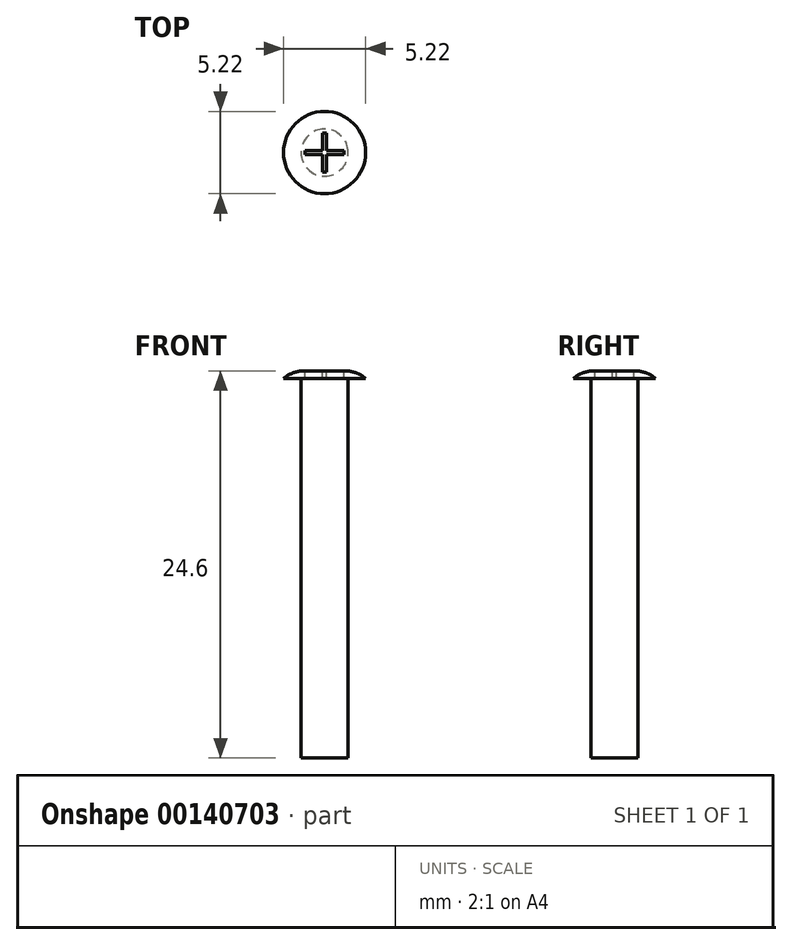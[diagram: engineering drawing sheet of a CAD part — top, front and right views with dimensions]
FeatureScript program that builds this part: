
annotation { "Feature Type Name" : "Feature", "Feature Type Description" : "" }
export const myFeature = defineFeature(function(context is Context, id is Id, definition is map)
    precondition{}
    {
        {
            var Q0;
            Q0=qCreatedBy(makeId("Top.planeOp"),FACE);
            var sketch = newSketch(context, id + "F0", { "sketchPlane" : qUnion([Q0])});
            skCircle(sketch, "E0", {"center": v(0, 0) * mm, "radius": 1.5 * mm});
            skSolve(sketch);
        }
        {
            var Q0;
            Q0=makeQuery(id+"F0.imprint","IMPRINT",FACE,{"disambiguationData":[TD([[makeQuery(id+"F0.imprint","IMPRINT",EDGE,{"derivedFrom":sQuery(id+"F0.wireOp",EDGE,"E0")}),1.0]])]});
            extrude(context, id + "F1", {"entities" : qUnion([Q0]), "depth" : 24.6 * mm});
        }
        {
            var Q0;
            Q0=makeQuery(id+"F1.opExtrude","CAP_FACE",FACE,{"disambiguationData":[OSD([sQuery(id+"F0.wireOp",EDGE,"E0")])],"isStart":false});
            var sketch = newSketch(context, id + "F2", { "sketchPlane" : qUnion([Q0])});
            skCircle(sketch, "E1.0", {"center": v(0, 0) * mm, "radius": 1.5 * mm});
            skCircle(sketch, "E2", {"center": v(0, 0) * mm, "radius": 2.6 * mm});
            skLineSegment(sketch, "E3", {"start": v(-1.25, -0.12) * mm, "end": v(-0.12, -0.12) * mm});
            skLineSegment(sketch, "E4", {"start": v(-1.25, 0.12) * mm, "end": v(-0.12, 0.12) * mm});
            skLineSegment(sketch, "E5", {"start": v(-0.12, -1.25) * mm, "end": v(-0.12, -0.12) * mm});
            skLineSegment(sketch, "E6", {"start": v(0.12, -1.25) * mm, "end": v(0.12, -0.12) * mm});
            skLineSegment(sketch, "E7.trimOffspring", {"start": v(-0.12, 0.12) * mm, "end": v(-0.12, 1.25) * mm});
            skLineSegment(sketch, "E8.trimOffspring", {"start": v(0.12, -0.12) * mm, "end": v(1.25, -0.12) * mm});
            skLineSegment(sketch, "E9.trimOffspring", {"start": v(0.12, 0.12) * mm, "end": v(1.25, 0.12) * mm});
            skLineSegment(sketch, "E10.trimOffspring", {"start": v(0.12, 0.12) * mm, "end": v(0.12, 1.25) * mm});
            skLineSegment(sketch, "E11", {"start": v(-1.25, -0.12) * mm, "end": v(-1.25, 0.12) * mm});
            skLineSegment(sketch, "E12", {"start": v(-0.12, -1.25) * mm, "end": v(0.12, -1.25) * mm});
            skLineSegment(sketch, "E13", {"start": v(1.25, -0.12) * mm, "end": v(1.25, 0.12) * mm});
            skLineSegment(sketch, "E14", {"start": v(-0.12, 1.25) * mm, "end": v(0.12, 1.25) * mm});
            skSolve(sketch);
        }
        {
            var Q0;
            Q0=qSketchRegion(id+"F2",true);
            extrude(context, id + "F3", {"entities" : qUnion([Q0]), "operationType" : NewBodyOperationType.ADD, "oppositeDirection" : true, "depth" : 0.5 * mm});
        }
        {
            var Q0;
            Q0=makeQuery(id+"F3.opExtrude","CAP_EDGE",EDGE,{"disambiguationData":[OSD([sQuery(id+"F2.wireOp",EDGE,"E2")])],"isStart":true});
            fillet(context, id + "F4", {"entities" : qUnion([Q0]), "radius" : 2 * mm, "tangentPropagation" : true, "allowEdgeOverflow" : false});
        }
        {
            var Q0;
            Q0=makeQuery(id+"F2.imprint","IMPRINT",FACE,{"disambiguationData":[TD([[makeQuery(id+"F2.imprint","IMPRINT",EDGE,{"derivedFrom":sQuery(id+"F2.wireOp",EDGE,"E3")}),1.0]])]});
            extrude(context, id + "F5", {"entities" : qUnion([Q0]), "operationType" : NewBodyOperationType.REMOVE, "oppositeDirection" : true, "depth" : 0.5 * mm});
        }
    });
